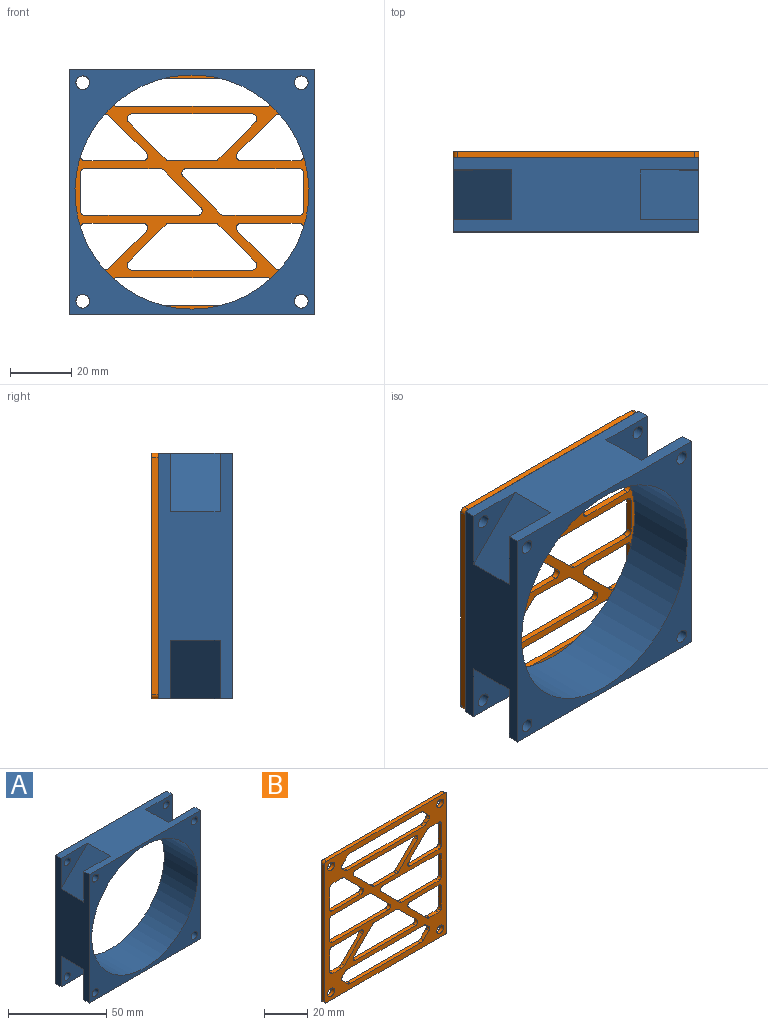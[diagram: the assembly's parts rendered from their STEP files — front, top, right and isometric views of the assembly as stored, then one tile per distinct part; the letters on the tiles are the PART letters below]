
ASSEMBLY  parts=2 mates=1
PART A: 27 faces, bbox 79.9x24.1x79.9 mm
  f0: cylinder r=2.22mm len=4.45mm, axis (0,1,0), area 55mm2, adj f14,f22
  f1: cylinder r=2.22mm len=4.45mm, axis (0,1,0), area 55mm2, adj f14,f19
  f2: cylinder r=2.22mm len=4.45mm, axis (0,1,0), area 55mm2, adj f14,f16
  f3: cylinder r=2.22mm len=4.45mm, axis (0,1,0), area 55mm2, adj f14,f25
  f4: plane 79.88x24.13mm, normal (-1,0,0), area 1308.2mm2, adj f5,f10,f13,f14,f15,f16,f17,f24
  f5: plane 79.88x24.13mm, normal (0,0,-1), area 1308.2mm2, adj f4,f6,f13,f14,f21,f22,f23,f24
  f6: plane 79.88x24.13mm, normal (1,0,0), area 1308.2mm2, adj f5,f10,f13,f14,f18,f19,f20,f21
  f7: cylinder r=2.22mm len=4.45mm, axis (0,1,0), area 55mm2, adj f13,f23
  f8: cylinder r=2.22mm len=4.45mm, axis (0,1,0), area 55mm2, adj f13,f20
  f9: cylinder r=38.1mm len=76.2mm, axis (0,1,0), area 5776.5mm2, adj f13,f14
  f10: plane 79.88x24.13mm, normal (0,0,1), area 1308.2mm2, adj f4,f6,f13,f14,f15,f16,f17,f18
  f11: cylinder r=2.22mm len=4.45mm, axis (0,1,0), area 55mm2, adj f13,f17
  f12: cylinder r=2.22mm len=4.45mm, axis (0,1,0), area 55mm2, adj f13,f26
  f13: plane 79.88x79.88mm, normal (0,-1,0), area 1758.9mm2, adj f4,f5,f6,f7,f8,f9,f10,f11
  f14: plane 79.88x79.88mm, normal (0,1,0), area 1758.9mm2, adj f0,f1,f2,f3,f4,f5,f6,f9
  f15: plane 19.05x19.05mm, normal (-0.71,0,0.71), area 437.9mm2, adj f4,f10,f16,f17
  f16: plane 19.05x19.05mm, normal (0,-1,0), area 165.9mm2, adj f2,f4,f10,f15
  f17: plane 19.05x19.05mm, normal (0,1,0), area 165.9mm2, adj f4,f10,f11,f15
  f18: plane 19.05x19.05mm, normal (0.71,0,0.71), area 437.9mm2, adj f6,f10,f19,f20
  f19: plane 19.05x19.05mm, normal (0,-1,0), area 165.9mm2, adj f1,f6,f10,f18
  f20: plane 19.05x19.05mm, normal (0,1,0), area 165.9mm2, adj f6,f8,f10,f18
  f21: plane 19.05x19.05mm, normal (0.71,0,-0.71), area 437.9mm2, adj f5,f6,f22,f23
  f22: plane 19.05x19.05mm, normal (0,-1,0), area 165.9mm2, adj f0,f5,f6,f21
  f23: plane 19.05x19.05mm, normal (0,1,0), area 165.9mm2, adj f5,f6,f7,f21
  f24: plane 19.05x19.05mm, normal (-0.71,0,-0.71), area 437.9mm2, adj f4,f5,f25,f26
  f25: plane 19.05x19.05mm, normal (0,-1,0), area 165.9mm2, adj f3,f4,f5,f24
  f26: plane 19.05x19.05mm, normal (0,1,0), area 165.9mm2, adj f4,f5,f12,f24
PART B: 106 faces, bbox 79.9x2x79.9 mm
  f0: plane 39.13x2.03mm, normal (0,0,1), area 79.5mm2, adj f52,f53,f90,f91
  f1: plane 12.19x12.19mm, normal (0.71,0,-0.71), area 35mm2, adj f52,f53,f90,f99
  f2: plane 14.75x2.03mm, normal (0,0,-1), area 30mm2, adj f52,f53,f99,f100
  f3: plane 12.19x12.19mm, normal (0.71,0,0.71), area 35mm2, adj f52,f53,f86,f93
  f4: plane 39.13x2.03mm, normal (0,0,-1), area 79.5mm2, adj f52,f53,f86,f87
  f5: plane 12.19x12.19mm, normal (-0.71,0,0.71), area 35mm2, adj f52,f53,f87,f95
  f6: plane 36.65x2.03mm, normal (0,0,-1), area 74.5mm2, adj f52,f53,f83,f94
  f7: plane 12.19x2.03mm, normal (-1,0,0), area 24.8mm2, adj f52,f53,f83,f84
  f8: plane 24.46x2.03mm, normal (0,0,1), area 49.7mm2, adj f52,f53,f84,f98
  f9: plane 11.71x2.03mm, normal (-1,0,0), area 23.8mm2, adj f52,f53,f64,f82
  f10: plane 18.87x2.03mm, normal (0,0,1), area 38.3mm2, adj f52,f53,f82,f96
  f11: plane 11.89x11.89mm, normal (0.71,0,-0.71), area 34.2mm2, adj f52,f53,f67,f96
  f12: plane 11.71x2.03mm, normal (-1,0,0), area 23.8mm2, adj f52,f53,f62,f81
  f13: plane 5.77x2.03mm, normal (0,0,1), area 11.7mm2, adj f52,f53,f61,f70
  f14: plane 11.89x11.89mm, normal (0.71,0,0.71), area 34.2mm2, adj f52,f53,f70,f101
  f15: plane 45.9x2.03mm, normal (0,0,1), area 93.3mm2, adj f52,f53,f59,f60
  f16: plane 3.51x3.51mm, normal (0.71,0,0.71), area 10.1mm2, adj f52,f53,f59,f79
  f17: plane 2.03x1.73mm, normal (0.71,0,-0.71), area 5mm2, adj f52,f53,f72,f79
  f18: plane 49.47x2.03mm, normal (0,0,-1), area 100.5mm2, adj f52,f53,f72,f73
  f19: plane 2.03x1.73mm, normal (-0.71,0,-0.71), area 5mm2, adj f52,f53,f73,f80
  f20: plane 11.71x2.03mm, normal (1,0,0), area 23.8mm2, adj f52,f53,f58,f78
  f21: plane 18.87x2.03mm, normal (0,0,-1), area 38.3mm2, adj f52,f53,f78,f92
  f22: plane 11.89x11.89mm, normal (-0.71,0,0.71), area 34.2mm2, adj f52,f53,f71,f92
  f23: plane 5.77x2.03mm, normal (0,0,1), area 11.7mm2, adj f52,f53,f57,f71
  f24: plane 12.19x2.03mm, normal (1,0,0), area 24.8mm2, adj f52,f53,f76,f77
  f25: plane 24.46x2.03mm, normal (0,0,-1), area 49.7mm2, adj f52,f53,f76,f88
  f26: plane 12.19x12.19mm, normal (-0.71,0,-0.71), area 35mm2, adj f52,f53,f88,f97
  f27: plane 76.84x2.03mm, normal (-1,0,0), area 156.1mm2, adj f52,f53,f102,f103
  f28: plane 76.84x2.03mm, normal (0,0,-1), area 156.1mm2, adj f52,f53,f103,f104
  f29: plane 76.84x2.03mm, normal (1,0,0), area 156.1mm2, adj f52,f53,f104,f105
  f30: plane 2.03x1.73mm, normal (0.71,0,0.71), area 5mm2, adj f52,f53,f68,f74
  f31: plane 3.51x3.51mm, normal (0.71,0,-0.71), area 10.1mm2, adj f52,f53,f56,f74
  f32: plane 45.9x2.03mm, normal (0,0,-1), area 93.3mm2, adj f52,f53,f56,f65
  f33: plane 3.51x3.51mm, normal (-0.71,0,-0.71), area 10.1mm2, adj f52,f53,f65,f85
  f34: plane 2.03x1.73mm, normal (-0.71,0,0.71), area 5mm2, adj f52,f53,f69,f85
  f35: plane 11.71x2.03mm, normal (1,0,0), area 23.8mm2, adj f52,f53,f55,f75
  f36: plane 5.77x2.03mm, normal (0,0,-1), area 11.7mm2, adj f52,f53,f54,f66
  f37: plane 11.89x11.89mm, normal (-0.71,0,-0.71), area 34.2mm2, adj f52,f53,f66,f89
  f38: plane 14.75x2.03mm, normal (0,0,1), area 30mm2, adj f52,f53,f93,f95
  f39: cylinder r=2.22mm len=4.45mm, axis (0,-1,0), area 28.4mm2, adj f52,f53
  f40: plane 12.19x12.19mm, normal (0.71,0,0.71), area 35mm2, adj f52,f53,f94,f98
  f41: plane 5.77x2.03mm, normal (0,0,-1), area 11.7mm2, adj f52,f53,f63,f67
  f42: cylinder r=2.22mm len=4.45mm, axis (0,-1,0), area 28.4mm2, adj f52,f53
  f43: plane 18.87x2.03mm, normal (0,0,-1), area 38.3mm2, adj f52,f53,f81,f101
  f44: cylinder r=2.22mm len=4.45mm, axis (0,-1,0), area 28.4mm2, adj f52,f53
  f45: plane 3.51x3.51mm, normal (-0.71,0,0.71), area 10.1mm2, adj f52,f53,f60,f80
  f46: plane 36.65x2.03mm, normal (0,0,1), area 74.5mm2, adj f52,f53,f77,f97
  f47: plane 76.84x2.03mm, normal (0,0,1), area 156.1mm2, adj f52,f53,f102,f105
  f48: cylinder r=2.22mm len=4.45mm, axis (0,-1,0), area 28.4mm2, adj f52,f53
  f49: plane 49.47x2.03mm, normal (0,0,1), area 100.5mm2, adj f52,f53,f68,f69
  f50: plane 18.87x2.03mm, normal (0,0,1), area 38.3mm2, adj f52,f53,f75,f89
  f51: plane 12.19x12.19mm, normal (-0.71,0,-0.71), area 35mm2, adj f52,f53,f91,f100
  f52: plane 79.88x79.88mm, normal (0,1,0), area 2397.1mm2, adj f0,f1,f2,f3,f4,f5,f6,f7
  f53: plane 79.88x79.88mm, normal (0,-1,0), area 2397.1mm2, adj f0,f1,f2,f3,f4,f5,f6,f7
  f54: cylinder r=2.54mm len=2.03mm, axis (0,1,0), area 3.3mm2, adj f36,f52,f53,f55
  f55: cylinder r=2.54mm len=2.03mm, axis (0,-1,0), area 3.3mm2, adj f35,f52,f53,f54
  f56: cylinder r=2.54mm len=2.03mm, axis (0,1,0), area 4.1mm2, adj f31,f32,f52,f53
  f57: cylinder r=2.54mm len=2.03mm, axis (0,-1,0), area 3.3mm2, adj f23,f52,f53,f58
  f58: cylinder r=2.54mm len=2.03mm, axis (0,-1,0), area 3.3mm2, adj f20,f52,f53,f57
  f59: cylinder r=2.54mm len=2.03mm, axis (0,-1,0), area 4.1mm2, adj f15,f16,f52,f53
  f60: cylinder r=2.54mm len=2.03mm, axis (0,-1,0), area 4.1mm2, adj f15,f45,f52,f53
  f61: cylinder r=2.54mm len=2.03mm, axis (0,-1,0), area 3.3mm2, adj f13,f52,f53,f62
  f62: cylinder r=2.54mm len=2.03mm, axis (0,1,0), area 3.3mm2, adj f12,f52,f53,f61
  f63: cylinder r=2.54mm len=2.03mm, axis (0,1,0), area 3.3mm2, adj f41,f52,f53,f64
  f64: cylinder r=2.54mm len=2.03mm, axis (0,1,0), area 3.3mm2, adj f9,f52,f53,f63
  f65: cylinder r=2.54mm len=2.03mm, axis (0,1,0), area 4.1mm2, adj f32,f33,f52,f53
  f66: cylinder r=2.54mm len=2.03mm, axis (0,1,0), area 4.1mm2, adj f36,f37,f52,f53
  f67: cylinder r=2.54mm len=2.03mm, axis (0,1,0), area 4.1mm2, adj f11,f41,f52,f53
  f68: cylinder r=2.54mm len=2.03mm, axis (0,-1,0), area 4.1mm2, adj f30,f49,f52,f53
  f69: cylinder r=2.54mm len=2.03mm, axis (0,-1,0), area 4.1mm2, adj f34,f49,f52,f53
  f70: cylinder r=2.54mm len=2.03mm, axis (0,-1,0), area 4.1mm2, adj f13,f14,f52,f53
  f71: cylinder r=2.54mm len=2.03mm, axis (0,-1,0), area 4.1mm2, adj f22,f23,f52,f53
  f72: cylinder r=2.54mm len=2.03mm, axis (0,1,0), area 4.1mm2, adj f17,f18,f52,f53
  f73: cylinder r=2.54mm len=2.03mm, axis (0,1,0), area 4.1mm2, adj f18,f19,f52,f53
  f74: cylinder r=1.52mm len=2.16mm, axis (0,1,0), area 4.9mm2, adj f30,f31,f52,f53
  f75: cylinder r=1.52mm len=2.03mm, axis (0,1,0), area 4.9mm2, adj f35,f50,f52,f53
  f76: cylinder r=1.52mm len=2.03mm, axis (0,-1,0), area 4.9mm2, adj f24,f25,f52,f53
  f77: cylinder r=1.52mm len=2.03mm, axis (0,1,0), area 4.9mm2, adj f24,f46,f52,f53
  f78: cylinder r=1.52mm len=2.03mm, axis (0,-1,0), area 4.9mm2, adj f20,f21,f52,f53
  f79: cylinder r=1.52mm len=2.16mm, axis (0,1,0), area 4.9mm2, adj f16,f17,f52,f53
  f80: cylinder r=1.52mm len=2.16mm, axis (0,1,0), area 4.9mm2, adj f19,f45,f52,f53
  f81: cylinder r=1.52mm len=2.03mm, axis (0,1,0), area 4.9mm2, adj f12,f43,f52,f53
  f82: cylinder r=1.52mm len=2.03mm, axis (0,-1,0), area 4.9mm2, adj f9,f10,f52,f53
  f83: cylinder r=1.52mm len=2.03mm, axis (0,1,0), area 4.9mm2, adj f6,f7,f52,f53
  f84: cylinder r=1.52mm len=2.03mm, axis (0,-1,0), area 4.9mm2, adj f7,f8,f52,f53
  f85: cylinder r=1.52mm len=2.16mm, axis (0,1,0), area 4.9mm2, adj f33,f34,f52,f53
  f86: cylinder r=1.52mm len=2.6mm, axis (0,1,0), area 7.3mm2, adj f3,f4,f52,f53
  f87: cylinder r=1.52mm len=2.6mm, axis (0,1,0), area 7.3mm2, adj f4,f5,f52,f53
  f88: cylinder r=1.52mm len=2.03mm, axis (0,1,0), area 2.4mm2, adj f25,f26,f52,f53
  f89: cylinder r=1.52mm len=2.6mm, axis (0,-1,0), area 7.3mm2, adj f37,f50,f52,f53
  f90: cylinder r=1.52mm len=2.6mm, axis (0,-1,0), area 7.3mm2, adj f0,f1,f52,f53
  f91: cylinder r=1.52mm len=2.6mm, axis (0,-1,0), area 7.3mm2, adj f0,f51,f52,f53
  f92: cylinder r=1.52mm len=2.6mm, axis (0,1,0), area 7.3mm2, adj f21,f22,f52,f53
  f93: cylinder r=1.52mm len=2.03mm, axis (0,-1,0), area 2.4mm2, adj f3,f38,f52,f53
  f94: cylinder r=1.52mm len=2.6mm, axis (0,1,0), area 7.3mm2, adj f6,f40,f52,f53
  f95: cylinder r=1.52mm len=2.03mm, axis (0,-1,0), area 2.4mm2, adj f5,f38,f52,f53
  f96: cylinder r=1.52mm len=2.6mm, axis (0,-1,0), area 7.3mm2, adj f10,f11,f52,f53
  f97: cylinder r=1.52mm len=2.6mm, axis (0,-1,0), area 7.3mm2, adj f26,f46,f52,f53
  f98: cylinder r=1.52mm len=2.03mm, axis (0,-1,0), area 2.4mm2, adj f8,f40,f52,f53
  f99: cylinder r=1.52mm len=2.03mm, axis (0,1,0), area 2.4mm2, adj f1,f2,f52,f53
  f100: cylinder r=1.52mm len=2.03mm, axis (0,1,0), area 2.4mm2, adj f2,f51,f52,f53
  f101: cylinder r=1.52mm len=2.6mm, axis (0,1,0), area 7.3mm2, adj f14,f43,f52,f53
  f102: cylinder r=1.52mm len=2.03mm, axis (0,1,0), area 4.9mm2, adj f27,f47,f52,f53
  f103: cylinder r=1.52mm len=2.03mm, axis (0,-1,0), area 4.9mm2, adj f27,f28,f52,f53
  f104: cylinder r=1.52mm len=2.03mm, axis (0,1,0), area 4.9mm2, adj f28,f29,f52,f53
  f105: cylinder r=1.52mm len=2.03mm, axis (0,-1,0), area 4.9mm2, adj f29,f47,f52,f53
PLACE A rot(axis=(0.71,0,-0.71),180deg) t=(-53.13,-55.41,-17.47)mm
PLACE B t=(-53.12,-42.33,-17.45)mm
MATE fastened A.f2 <-> B.f48  axis (0,1,0) through (-88.69,-43.34,18.09)mm
